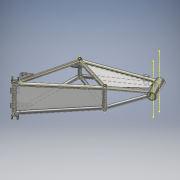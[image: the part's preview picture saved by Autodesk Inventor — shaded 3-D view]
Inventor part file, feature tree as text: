
AUTODESK INVENTOR PART (.ipt)
format: ipt  version: 2019.3 (Build 233278000, 278)  size: 607,744 bytes
history: native  units: mm
features: other x13, plane x5, extrude x4, sketch x4, mirror x2, hole x1, fillet x1, boolean_combine x1, delete_face x1, thicken_offset x1
ambient origin geometry x8: Origin, YZ Plane, XZ Plane, XY Plane, X Axis, Y Axis, Z Axis, Center Point
bodies: Solid1 (feature_tree), Solid2 (feature_tree), Solid3 (feature_tree), Solid4 (feature_tree), Solid5 (feature_tree), Solid6 (feature_tree), Solid11 (feature_tree)
feature tree (33):
  other  "MainFrame.ipt"
  plane  "Work Plane1"
  extrude  "Extrusion1"  Depth=2.0mm
  plane  "Work Plane2"
  plane  "Work Plane3"
  extrude  "Extrusion3"  Depth=45.0mm
  hole  "Hole1"  [1 undecoded]
  mirror  "Mirror1"
  fillet  "Fillet1"  Radius=30.0mm
  mirror  "Mirror2"
  plane  "Work Plane6"
  extrude  "Extrusion4"  Depth=2.0mm
  boolean_combine  "Combine2"
  delete_face  "Delete Face2"
  thicken_offset  "Thicken2"
  plane  "Work Plane9"
  extrude  "Extrusion6"  Depth=2.0mm
  other  "Frame::MainFrame.ipt"
  other  "PivotPlateRight::MainFrame.ipt"
  other  "ShockPlateRight::MainFrame.ipt"
  other  "PivotPlateLeft::MainFrame.ipt"
  other  "FootpegRight::MainFrame.ipt"
  other  "FootpegLeft::MainFrame.ipt"
  other  "TaggingFeature1"
  sketch  "Sketch1"  dims[d0=10.0mm d1=2.0mm]
  other  "BatteryFloor"
  sketch  "Sketch4"  dims[d2=3.0mm d3=0.0mm d7=45.0mm]
  other  "Hinge"
  sketch  "Sketch8"  dims[d8=1.0mm d9=16.0mm d10=30.0mm d11=0.0mm]
  other  "ToptubeMiniPanel"
  other  "HeadTube::MainFrame.ipt"
  sketch  "Sketch12"  dims[d24=10.0mm d25=10.0mm d14=5.5mm d15=6.0mm d16=4.0mm d17=2.0mm d18=90.0deg d19=8.25mm d20=20.594885mm d23=2.0mm d26=5.0mm d28=50.0mm d29=30.0mm d30=16.5mm d31=0.0mm d37=1.5mm d38=1.5mm d39=2.0mm d40=0.0mm]
  other  "CableBoxRight"
note: 1 required parameter value undecoded (feature->parameter linkage not recoverable at this tier; creation-order binding heuristic only, values carry confidence <= 0.55)
